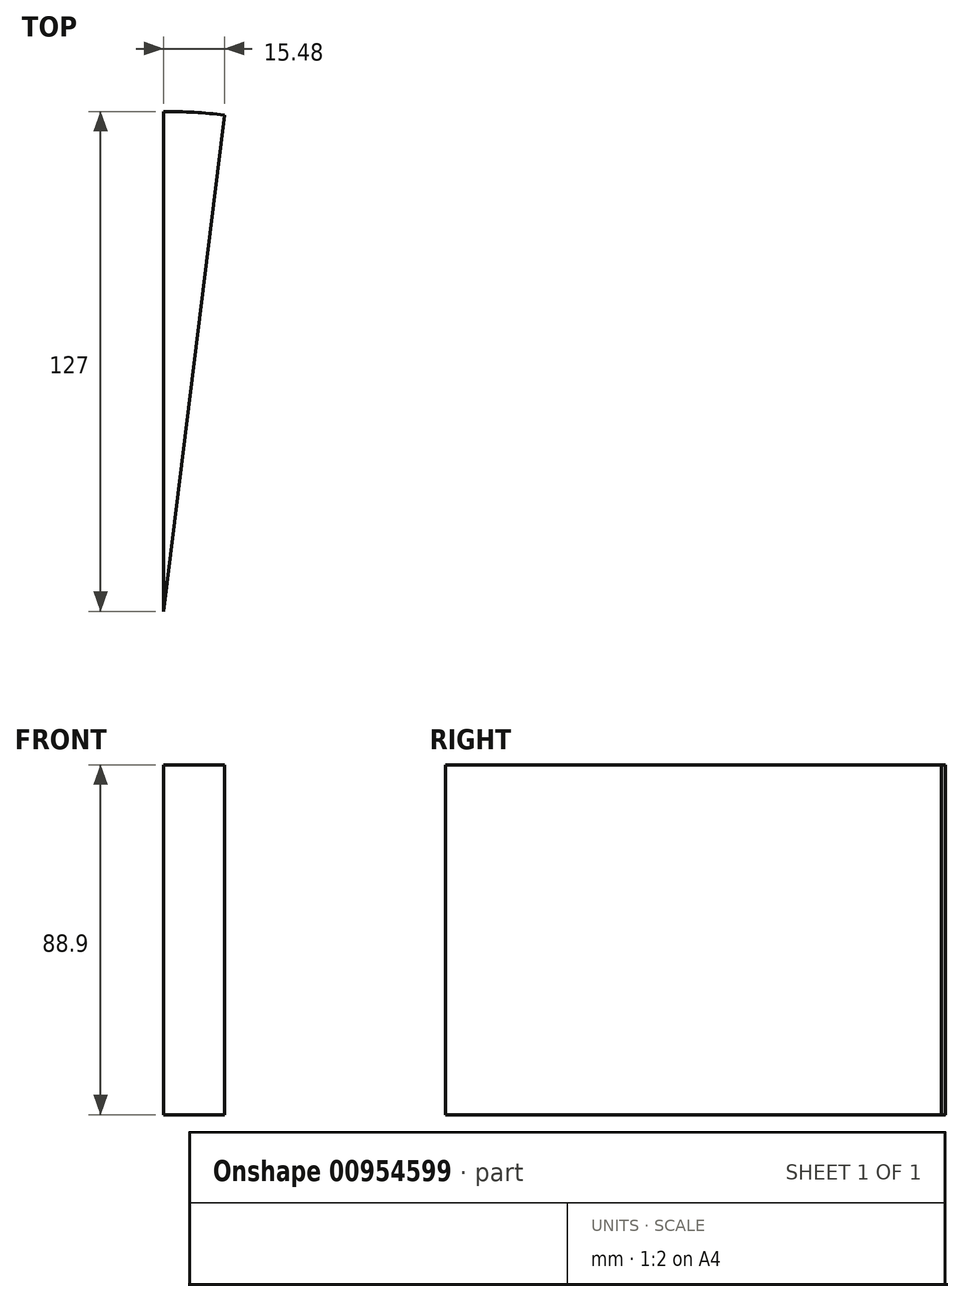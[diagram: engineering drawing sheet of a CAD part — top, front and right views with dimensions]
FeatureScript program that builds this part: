
annotation { "Feature Type Name" : "Feature", "Feature Type Description" : "" }
export const myFeature = defineFeature(function(context is Context, id is Id, definition is map)
    precondition{}
    {
        {
            var Q0;
            Q0=qCreatedBy(makeId("Top.planeOp"),FACE);
            var sketch = newSketch(context, id + "F0", { "sketchPlane" : qUnion([Q0])});
            skCircle(sketch, "E0", {"center": v(0, 0) * mm, "radius": 127 * mm});
            skSolve(sketch);
        }
        {
            var Q0;
            Q0=qCreatedBy(makeId("Top.planeOp"),FACE);
            var sketch = newSketch(context, id + "F1", { "sketchPlane" : qUnion([Q0])});
            skLineSegment(sketch, "E1", {"start": v(0, 0) * mm, "end": v(0, 127) * mm});
            skLineSegment(sketch, "E2", {"start": v(15.48, 126.05) * mm, "end": v(0, 0) * mm});
            skArc(sketch, "E3.0", {"start": v(15.48, 126.05) * mm, "mid": v(7.75, 126.76) * mm, "end": v(0, 127) * mm});
            skSolve(sketch);
        }
        {
            var Q0;
            Q0=makeQuery(id+"F1.imprint","IMPRINT",FACE,{"disambiguationData":[TD([[makeQuery(id+"F1.imprint","IMPRINT",EDGE,{"derivedFrom":sQuery(id+"F1.wireOp",EDGE,"E1")}),-1.0]])]});
            extrude(context, id + "F2", {"entities" : qUnion([Q0]), "depth" : 88.9 * mm, "offsetDistance" : 25.4 * mm});
        }
    });
